# Revit family: CENTUM Wandwinkel 3-Loch, quer XL 80
name_source: partatom
category: HLS-Bauteile
units: mm (PartAtom-declared; Revit-internal decimal feet)

## family parameters
Arbeitsebenenbasiert = Ja
Beim Laden mit Abzugskörper schneiden = Nein
Bemaßung runder Anschluss = Durchmesser verwenden
Beschriftungsausrichtung beibehalten = Nein
Gemeinsam genutzt = Ja
Immer vertikal = Nein
Raumberechnungspunkt = Nein
Teiletyp = Normal

## types (1)
- CENTUM Wandwinkel 3-Loch, quer XL 80
    Artikelnummer = 1640101006
    B = 70 mm  [stored 0.229659 ft]
    Breite Material = 70 mm
    EAN = 4250928468826
    Fabrikat = MEFA
    Firma = MEFA Befestigungs- und Montagesysteme GmbH
    Gewicht = 1.14 kg
    Gewicht pro Bauteil = 1.14 kg
    Kurztext1 = CENTUM Wandwinkel 3-Loch
    Kurztext2 = 90 ° Schenkel 150 x 75 mm
    L1 = 150 mm
    L2 = 75 mm  [stored 0.246063 ft]
    Langloch = 14x40 mm
    Lochdurchmesser = 14 mm
    Länge Schenkel 1 = 150 mm
    Länge Schenkel 2 = 75 mm  [stored 0.246063 ft]
    Material = Stahl
    Materialname = S235
    Mengeneinheit = St
    Oberflaeche = feuerstückverzinkt
    Profil = CENTUM
    Profiltyp = XL 80
    S = 10 mm  [stored 0.0328084 ft]
    Sicherheitsfaktor = 1.54
    Stärke Material = 10 mm  [stored 0.0328084 ft]
    Vorgabe-Ansicht = 1219 mm
    Winkel = 90 °
    vpe = 1

note: [stored X ft] marks values corroborated as IEEE doubles in the binary element streams (Revit-internal decimal feet)
